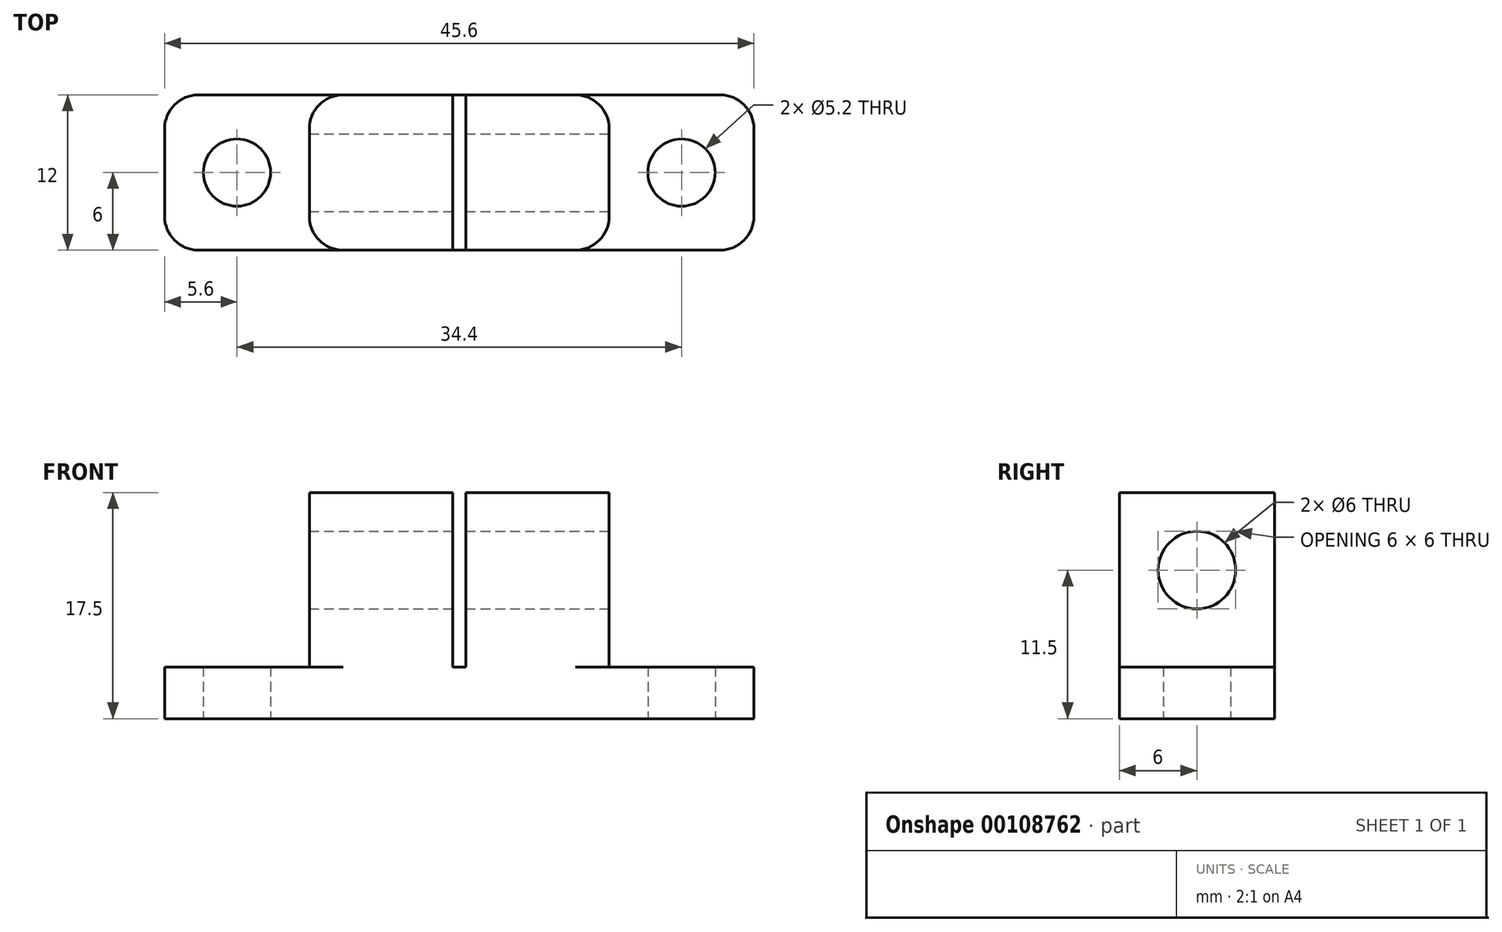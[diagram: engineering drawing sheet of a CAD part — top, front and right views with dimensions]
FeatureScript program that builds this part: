
annotation { "Feature Type Name" : "Feature", "Feature Type Description" : "" }
export const myFeature = defineFeature(function(context is Context, id is Id, definition is map)
    precondition{}
    {
        {
            assignVariable(context, id + "F0", {"name" : "RodD", "anyValue" : 6});
        }
        {
            assignVariable(context, id + "F1", {"name" : "BoltD", "anyValue" : 5.2});
        }
        {
            assignVariable(context, id + "F2", {"name" : "BaseThickness", "anyValue" : 4});
        }
        {
            var Q0;
            Q0=qCreatedBy(makeId("Top.planeOp"),FACE);
            var sketch = newSketch(context, id + "F3", { "sketchPlane" : qUnion([Q0])});
            skLineSegment(sketch, "E0.bottom", {"start": v(-22.8, 6) * mm, "end": v(22.8, 6) * mm});
            skLineSegment(sketch, "E0.top", {"start": v(-22.8, -6) * mm, "end": v(22.8, -6) * mm});
            skLineSegment(sketch, "E0.left", {"start": v(-22.8, 6) * mm, "end": v(-22.8, -6) * mm});
            skLineSegment(sketch, "E0.right", {"start": v(22.8, 6) * mm, "end": v(22.8, -6) * mm});
            skCircle(sketch, "E1", {"center": v(-17.2, 0) * mm, "radius": 2.6 * mm});
            skCircle(sketch, "E2", {"center": v(17.2, 0) * mm, "radius": 2.6 * mm});
            skSolve(sketch);
        }
        {
            var Q0;
            Q0=makeQuery(id+"F3.imprint","IMPRINT",FACE,{"disambiguationData":[TD([[makeQuery(id+"F3.imprint","IMPRINT",EDGE,{"derivedFrom":sQuery(id+"F3.wireOp",EDGE,"E0.bottom")}),-1.0]])]});
            extrude(context, id + "F4", {"entities" : qUnion([Q0]), "depth" : (getVariable(context, 'BaseThickness')) * mm});
        }
        {
            var Q0;
            Q0=makeQuery(id+"F4.opExtrude","CAP_FACE",FACE,{"disambiguationData":[OSD([sQuery(id+"F3.wireOp",EDGE,"E0.bottom"),sQuery(id+"F3.wireOp",EDGE,"E0.top"),sQuery(id+"F3.wireOp",EDGE,"E0.left"),sQuery(id+"F3.wireOp",EDGE,"E0.right"),sQuery(id+"F3.wireOp",EDGE,"E1"),sQuery(id+"F3.wireOp",EDGE,"E2")])],"isStart":false});
            var sketch = newSketch(context, id + "F5", { "sketchPlane" : qUnion([Q0])});
            skLineSegment(sketch, "E3.bottom", {"start": v(-11.6, 6) * mm, "end": v(11.6, 6) * mm});
            skLineSegment(sketch, "E3.top", {"start": v(-11.6, -6) * mm, "end": v(11.6, -6) * mm});
            skLineSegment(sketch, "E3.left", {"start": v(-11.6, 6) * mm, "end": v(-11.6, -6) * mm});
            skLineSegment(sketch, "E3.right", {"start": v(11.6, 6) * mm, "end": v(11.6, -6) * mm});
            skSolve(sketch);
        }
        {
            var Q0;
            Q0=makeQuery(id+"F5.imprint","IMPRINT",FACE,{"disambiguationData":[TD([[makeQuery(id+"F5.imprint","IMPRINT",EDGE,{"derivedFrom":sQuery(id+"F5.wireOp",EDGE,"E3.bottom")}),-1.0]])]});
            extrude(context, id + "F6", {"entities" : qUnion([Q0]), "operationType" : NewBodyOperationType.ADD, "depth" : (getVariable(context, 'RodD') * 2.25) * mm});
        }
        {
            var Q0;
            Q0=makeQuery(id+"F6.opExtrude","SWEPT_FACE",FACE,{"disambiguationData":[OSD([sQuery(id+"F5.wireOp",EDGE,"E3.right")])]});
            var sketch = newSketch(context, id + "F7", { "sketchPlane" : qUnion([Q0])});
            skCircle(sketch, "E4", {"center": v(0, 11.5) * mm, "radius": 3 * mm});
            skSolve(sketch);
        }
        {
            var Q0;
            Q0=makeQuery(id+"F7.imprint","IMPRINT",FACE,{"disambiguationData":[TD([[makeQuery(id+"F7.imprint","IMPRINT",EDGE,{"derivedFrom":sQuery(id+"F7.wireOp",EDGE,"E4")}),1.0]])]});
            var Q1;
            Q1=makeQuery(id+"F6.opExtrude","SWEPT_FACE",FACE,{"disambiguationData":[OSD([sQuery(id+"F5.wireOp",EDGE,"E3.left")])]});
            extrude(context, id + "F8", {"entities" : qUnion([Q0]), "operationType" : NewBodyOperationType.REMOVE, "endBound" : BoundingType.UP_TO_SURFACE, "oppositeDirection" : true, "endBoundEntityFace" : qUnion([Q1]), "depth" : 25 * mm});
        }
        {
            var Q0;
            Q0=makeQuery(id+"F6.opExtrude","CAP_FACE",FACE,{"disambiguationData":[OSD([sQuery(id+"F5.wireOp",EDGE,"E3.bottom"),sQuery(id+"F5.wireOp",EDGE,"E3.top"),sQuery(id+"F5.wireOp",EDGE,"E3.left"),sQuery(id+"F5.wireOp",EDGE,"E3.right")])],"isStart":false});
            var sketch = newSketch(context, id + "F9", { "sketchPlane" : qUnion([Q0])});
            skLineSegment(sketch, "E5.bottom", {"start": v(-0.5, 6) * mm, "end": v(0.5, 6) * mm});
            skLineSegment(sketch, "E5.top", {"start": v(-0.5, -6) * mm, "end": v(0.5, -6) * mm});
            skLineSegment(sketch, "E5.left", {"start": v(-0.5, 6) * mm, "end": v(-0.5, -6) * mm});
            skLineSegment(sketch, "E5.right", {"start": v(0.5, 6) * mm, "end": v(0.5, -6) * mm});
            skSolve(sketch);
        }
        {
            var Q0;
            Q0=makeQuery(id+"F9.imprint","IMPRINT",FACE,{"disambiguationData":[TD([[makeQuery(id+"F9.imprint","IMPRINT",EDGE,{"derivedFrom":sQuery(id+"F9.wireOp",EDGE,"E5.bottom")}),-1.0]])]});
            var Q1;
            {var subQ0=sQuery(id+"F3.wireOp",EDGE,"E0.bottom");var subQ1=sQuery(id+"F3.wireOp",EDGE,"E0.top");var subQ2=sQuery(id+"F3.wireOp",EDGE,"E0.left");var subQ3=sQuery(id+"F3.wireOp",EDGE,"E1");Q1=makeQuery(id+"F6.boolean.opBoolean","SPLIT",FACE,{"disambiguationData":[TD([makeQuery(id+"F4.opExtrude","SWEPT_FACE",FACE,{"disambiguationData":[OSD([subQ2])]})])],"derivedFrom":makeQuery(id+"F4.opExtrude","CAP_FACE",FACE,{"disambiguationData":[OSD([subQ0,subQ1,subQ2,sQuery(id+"F3.wireOp",EDGE,"E0.right"),subQ3,sQuery(id+"F3.wireOp",EDGE,"E2")])],"isStart":false})});}
            extrude(context, id + "F10", {"entities" : qUnion([Q0]), "operationType" : NewBodyOperationType.REMOVE, "endBound" : BoundingType.UP_TO_SURFACE, "oppositeDirection" : true, "endBoundEntityFace" : qUnion([Q1]), "depth" : 25 * mm});
        }
        {
            var Q0;
            Q0=makeQuery(id+"F4.opExtrude","SWEPT_EDGE",EDGE,{"disambiguationData":[OSD([sQuery(id+"F3.wireOp",EDGE,"E0.top"),sQuery(id+"F3.wireOp",EDGE,"E0.left")])]});
            var Q1;
            Q1=makeQuery(id+"F4.opExtrude","SWEPT_EDGE",EDGE,{"disambiguationData":[OSD([sQuery(id+"F3.wireOp",EDGE,"E0.bottom"),sQuery(id+"F3.wireOp",EDGE,"E0.left")])]});
            var Q2;
            Q2=makeQuery(id+"F4.opExtrude","SWEPT_EDGE",EDGE,{"disambiguationData":[OSD([sQuery(id+"F3.wireOp",EDGE,"E0.top"),sQuery(id+"F3.wireOp",EDGE,"E0.right")])]});
            var Q3;
            Q3=makeQuery(id+"F4.opExtrude","SWEPT_EDGE",EDGE,{"disambiguationData":[OSD([sQuery(id+"F3.wireOp",EDGE,"E0.bottom"),sQuery(id+"F3.wireOp",EDGE,"E0.right")])]});
            var Q4;
            Q4=makeQuery(id+"F6.opExtrude","SWEPT_EDGE",EDGE,{"disambiguationData":[OSD([sQuery(id+"F3.wireOp",EDGE,"E0.bottom"),sQuery(id+"F5.wireOp",EDGE,"E3.bottom"),sQuery(id+"F5.wireOp",EDGE,"E3.left")])]});
            var Q5;
            Q5=makeQuery(id+"F6.opExtrude","SWEPT_EDGE",EDGE,{"disambiguationData":[OSD([sQuery(id+"F3.wireOp",EDGE,"E0.top"),sQuery(id+"F5.wireOp",EDGE,"E3.top"),sQuery(id+"F5.wireOp",EDGE,"E3.left")])]});
            var Q6;
            Q6=makeQuery(id+"F6.opExtrude","SWEPT_EDGE",EDGE,{"disambiguationData":[OSD([sQuery(id+"F3.wireOp",EDGE,"E0.bottom"),sQuery(id+"F5.wireOp",EDGE,"E3.bottom"),sQuery(id+"F5.wireOp",EDGE,"E3.right")])]});
            var Q7;
            Q7=makeQuery(id+"F6.opExtrude","SWEPT_EDGE",EDGE,{"disambiguationData":[OSD([sQuery(id+"F3.wireOp",EDGE,"E0.top"),sQuery(id+"F5.wireOp",EDGE,"E3.top"),sQuery(id+"F5.wireOp",EDGE,"E3.right")])]});
            fillet(context, id + "F11", {"entities" : qUnion([Q0, Q1, Q2, Q3, Q4, Q5, Q6, Q7]), "radius" : (getVariable(context, 'BoltD') / 2) * mm, "tangentPropagation" : true, "allowEdgeOverflow" : false});
        }
    });
